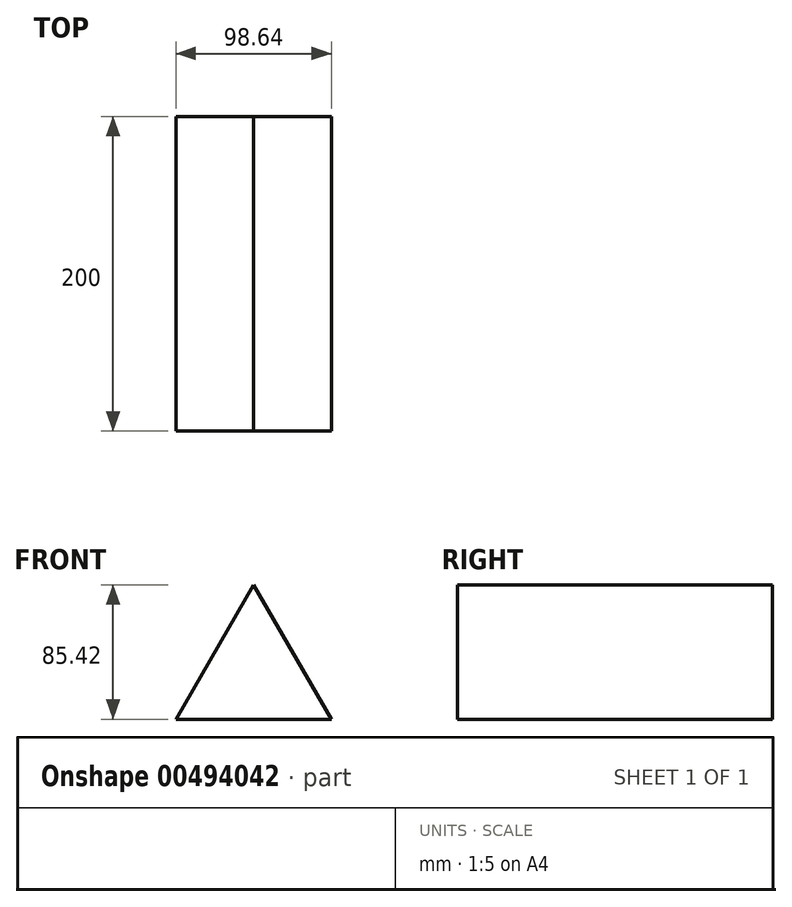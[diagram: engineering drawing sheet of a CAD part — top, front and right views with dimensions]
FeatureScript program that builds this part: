
annotation { "Feature Type Name" : "Feature", "Feature Type Description" : "" }
export const myFeature = defineFeature(function(context is Context, id is Id, definition is map)
    precondition{}
    {
        {
            var Q0;
            Q0=qCreatedBy(makeId("Front.planeOp"),FACE);
            var sketch = newSketch(context, id + "F0", { "sketchPlane" : qUnion([Q0])});
            skCircle(sketch, "E0.cCircle", {"center": v(0, 0) * mm, "radius": 56.95 * mm, "construction": true});
            skLineSegment(sketch, "E0.0", {"start": v(0, 56.95) * mm, "end": v(49.32, -28.47) * mm});
            skLineSegment(sketch, "E0.1", {"start": v(49.32, -28.47) * mm, "end": v(-49.32, -28.47) * mm});
            skLineSegment(sketch, "E0.2", {"start": v(-49.32, -28.47) * mm, "end": v(0, 56.95) * mm});
            skSolve(sketch);
        }
        {
            var Q0;
            Q0=makeQuery(id+"F0.imprint","IMPRINT",FACE,{"disambiguationData":[TD([[makeQuery(id+"F0.imprint","IMPRINT",EDGE,{"derivedFrom":sQuery(id+"F0.wireOp",EDGE,"E0.0")}),-1.0]])]});
            extrude(context, id + "F1", {"entities" : qUnion([Q0]), "depth" : 200 * mm});
        }
    });
